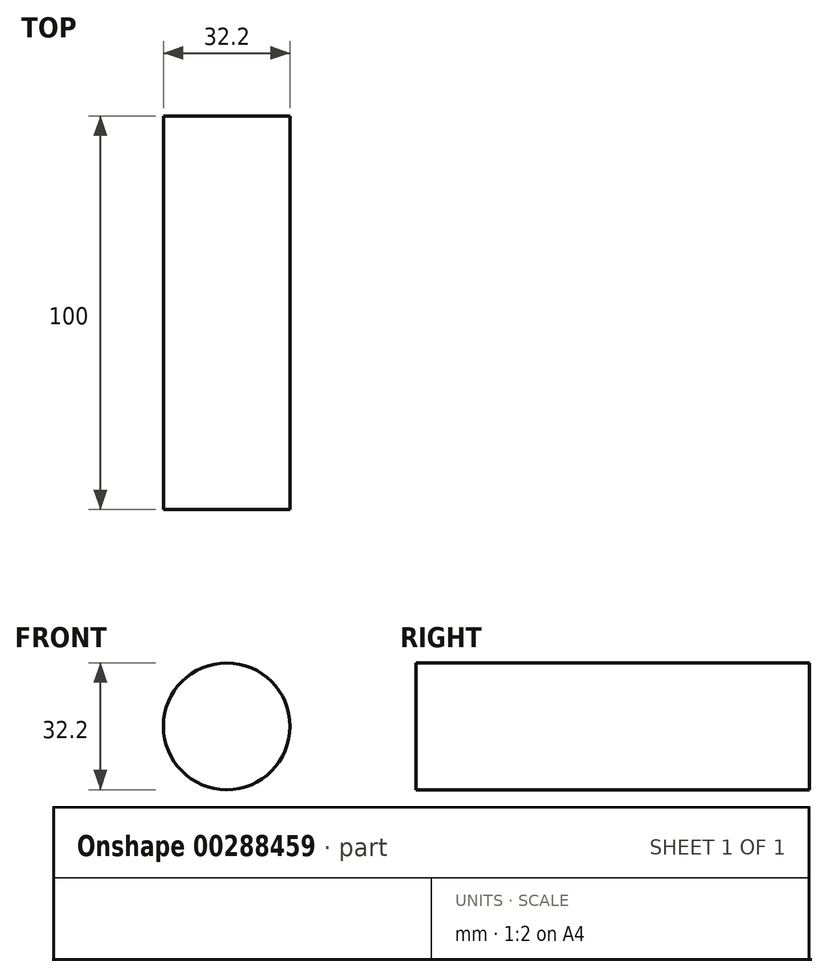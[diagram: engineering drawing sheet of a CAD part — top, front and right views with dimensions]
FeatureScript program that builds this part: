
annotation { "Feature Type Name" : "Feature", "Feature Type Description" : "" }
export const myFeature = defineFeature(function(context is Context, id is Id, definition is map)
    precondition{}
    {
        {
            var Q0;
            Q0=qCreatedBy(makeId("Front.planeOp"),FACE);
            var sketch = newSketch(context, id + "F0", { "sketchPlane" : qUnion([Q0])});
            skCircle(sketch, "E0", {"center": v(0, 0) * mm, "radius": 16.1 * mm});
            skSolve(sketch);
        }
        {
            var Q0;
            Q0=makeQuery(id+"F0.imprint","IMPRINT",FACE,{"disambiguationData":[TD([[makeQuery(id+"F0.imprint","IMPRINT",EDGE,{"derivedFrom":sQuery(id+"F0.wireOp",EDGE,"E0")}),1.0]])]});
            extrude(context, id + "F1", {"entities" : qUnion([Q0]), "depth" : 100 * mm});
        }
    });
